# Revit family: FP-Revit19-en-CI302DG1-CI392DG1-CI392DTTG1-CI604DTTG1-CI764DTTG1-CI905DTTG1-InductionCooktop-0-90003216A-AU-NZ-UK-IE-CN-SG-ASIA
name_source: partatom
category: Specialty Equipment
units: mm (PartAtom-declared; Revit-internal decimal feet)

## family parameters
Always vertical = Yes
Cut with Voids When Loaded = Yes
OmniClass Number = 23.40.40.14.17.11
OmniClass Title = Cookers, Ovens, Stoves
Part Type = Normal
Room Calculation Point = No
Round Connector Dimension = Use Diameter
Shared = No
Work Plane-Based = No

## types (7) — shared parameters
Cavity - Depth (Flush Mount) = 509 mm
Cavity - Depth (Proud Mount) = 507 mm
Cavity - Height = 72 mm  [stored 0.23622 ft]
Chassis - Depth = 504 mm
Chassis - Height = 56 mm  [stored 0.183727 ft]
Clearance - Overhead Non-Combustible = 450 mm  [stored 1.47638 ft]
Clearance - Overhead Rangehood = 650 mm  [stored 2.13255 ft]
Clearance - Rear Combustible = 20 mm  [stored 0.0656168 ft]
Clearance - Side Combustible = 27 mm  [stored 0.0885827 ft]
Manufacturer = Fisher & Paykel Appliances Ltd
Material - Body = Fisher & Paykel - Grey
Material - Display Panel = Fisher & Paykel - Grey, Charcoal
Material - Graphics = Fisher & Paykel - Grey, Charcoal
Product - Depth = 530 mm  [stored 1.73885 ft]
Product - Height = 62 mm  [stored 0.203412 ft]
Recess - Depth = 7 mm  [stored 0.0229659 ft]
Visibility - Clearance Required = Yes
Visibility - Power Conduit US-CA = No

## per-type parameters (varying)
| type | Cavity - Width | Chassis - Width | Connector Description - Electrical | Description | Graphics - 30/15 | Graphics - 39/17 | Graphics - 60/24 | Graphics - 76/30 | Graphics - 90/36 | Material - Cooktop | Model | Product - Width | Visibility - Power Flex Large | Visibility - Power Flex Small | Visibility - Touchscreen |
| CI905DTTB1 | 862 mm | 854 mm | 220-240V, 50Hz, 50A | 90cm, 5 Zone Induction Cooktop, Black, Touchscreen | No | No | No | No | Yes | Fisher & Paykel - Glass, Black | CI905DTTB1 | 900 mm  [stored 2.95276 ft] | Yes | No | Yes |
| CI302DG1 | 262 mm  [stored 0.85958 ft] | 254 mm  [stored 0.833333 ft] | 220-240V, 50Hz, 20A | 30cm, 2 Zone Induction Cooktop, Grey | Yes | No | No | No | No | Fisher & Paykel - Glass, Grey | CI302DG1 | 300 mm | No | Yes | No |
| CI392DG1 | 347 mm | 334 mm | 220-240V, 50Hz, 20A | 39cm, 2 Zone Induction Cooktop, Grey | No | Yes | No | No | No | Fisher & Paykel - Glass, Grey | CI392DG1 | 385 mm | No | Yes | No |
| CI392DTTG1 | 347 mm | 334 mm | 220-240V, 50Hz, 20A | 39cm, 2 Zone Induction Cooktop, Grey, Touchscreen | No | Yes | No | No | No | Fisher & Paykel - Glass, Grey | CI392DTTB1 | 385 mm | No | Yes | Yes |
| CI604DTTG1 | 562 mm | 554 mm | 220-240V, 50Hz, 35A | 60cm, 4 Zone Induction Cooktop, Grey, Touchscreen | No | No | Yes | No | No | Fisher & Paykel - Glass, Grey | CI604DTTB1 | 600 mm | Yes | No | Yes |
| CI764DTTG1 | 722 mm | 714 mm | 220-240V, 50Hz, 35A | 76cm, 4 Zone Induction Cooktop, Grey, Touchscreen | No | No | No | Yes | No | Fisher & Paykel - Glass, Grey | CI764DTTB1 | 760 mm | Yes | No | Yes |
| CI905DTTG1 | 862 mm | 854 mm | 220-240V, 50Hz, 50A | 90cm, 5 Zone Induction Cooktop, Grey, Touchscreen | No | No | No | No | Yes | Fisher & Paykel - Glass, Grey | CI905DTTG1 | 900 mm  [stored 2.95276 ft] | Yes | No | Yes |

note: [stored X ft] marks values corroborated as IEEE doubles in the binary element streams (Revit-internal decimal feet)

## geometry (parser evidence)
native form markers: Sweep x3
no freeform markers — native parametric forms only
